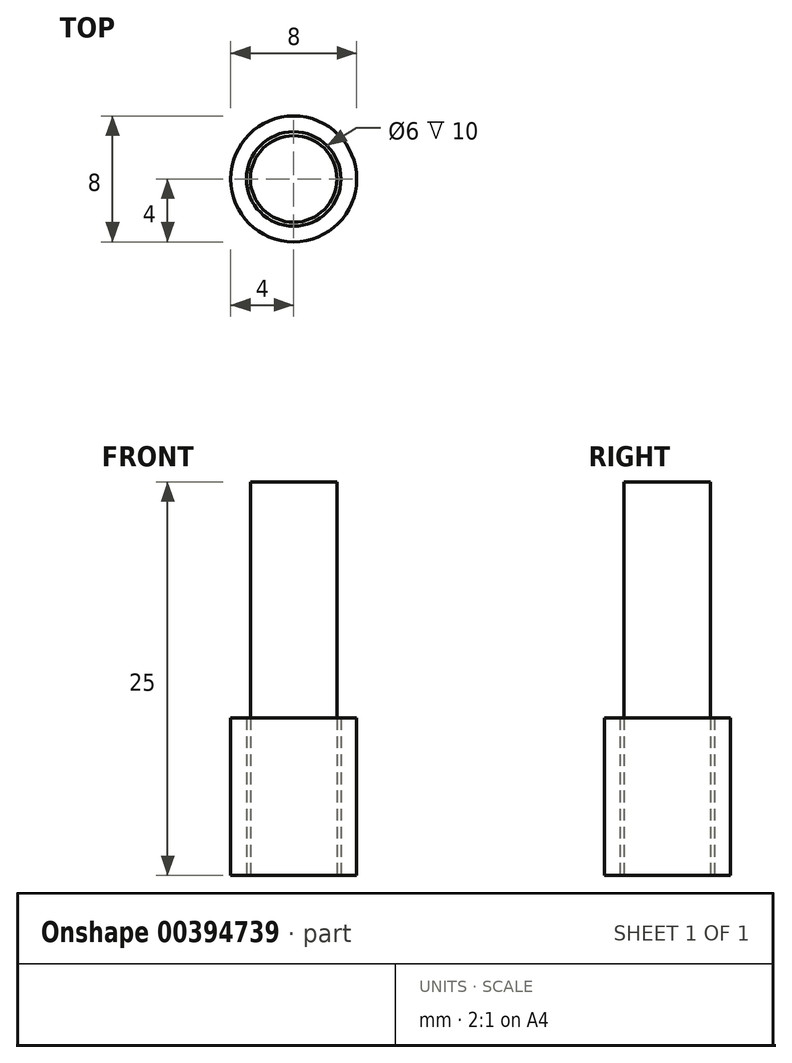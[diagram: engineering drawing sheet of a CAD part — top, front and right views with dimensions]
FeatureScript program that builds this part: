
annotation { "Feature Type Name" : "Feature", "Feature Type Description" : "" }
export const myFeature = defineFeature(function(context is Context, id is Id, definition is map)
    precondition{}
    {
        {
            var Q0;
            Q0=qCreatedBy(makeId("Top.planeOp"),FACE);
            var sketch = newSketch(context, id + "F0", { "sketchPlane" : qUnion([Q0])});
            skCircle(sketch, "E0", {"center": v(0, 0) * mm, "radius": 4 * mm});
            skCircle(sketch, "E1", {"center": v(0, 0) * mm, "radius": 3 * mm});
            skSolve(sketch);
        }
        {
            var Q0;
            Q0=makeQuery(id+"F0.imprint","IMPRINT",FACE,{"disambiguationData":[TD([[makeQuery(id+"F0.imprint","IMPRINT",EDGE,{"derivedFrom":sQuery(id+"F0.wireOp",EDGE,"E0")}),1.0]])]});
            extrude(context, id + "F1", {"entities" : qUnion([Q0]), "depth" : 10 * mm});
        }
        {
            var Q0;
            Q0=qCreatedBy(makeId("Top.planeOp"),FACE);
            var sketch = newSketch(context, id + "F2", { "sketchPlane" : qUnion([Q0])});
            skCircle(sketch, "E2", {"center": v(0, 0) * mm, "radius": 2.75 * mm});
            skSolve(sketch);
        }
        {
            var Q0;
            Q0=makeQuery(id+"F2.imprint","IMPRINT",FACE,{"disambiguationData":[TD([[makeQuery(id+"F2.imprint","IMPRINT",EDGE,{"derivedFrom":sQuery(id+"F2.wireOp",EDGE,"E2")}),1.0]])]});
            var Q1;
            Q1=sQuery(id+"F2.wireOp",EDGE,"E2");
            extrude(context, id + "F3", {"entities" : qUnion([Q0]), "surfaceEntities" : qUnion([Q1]), "depth" : 25 * mm});
        }
    });
